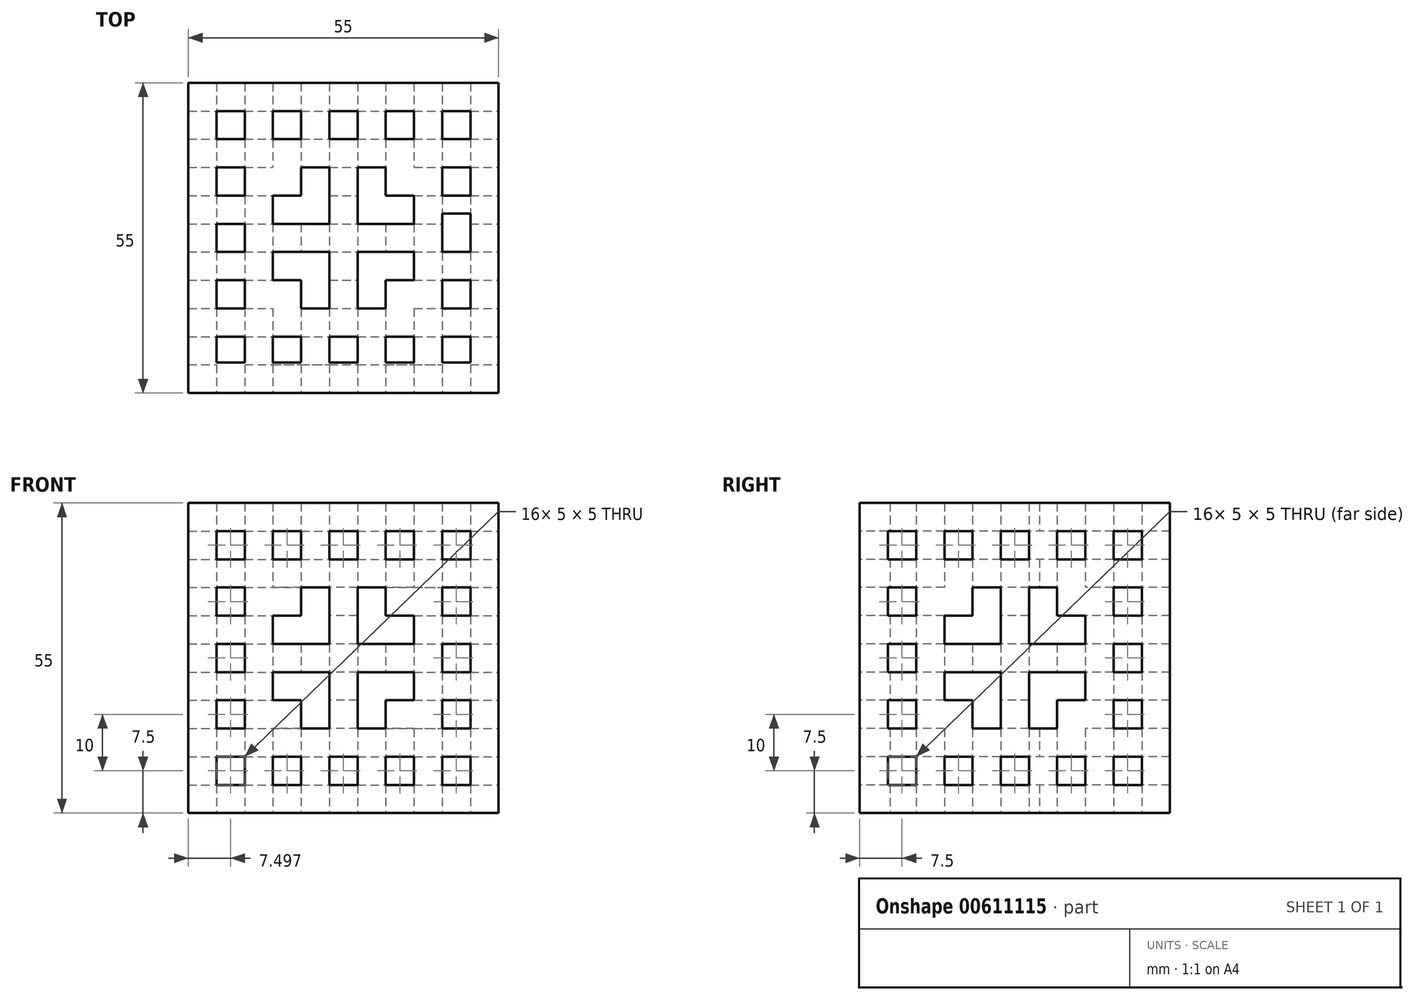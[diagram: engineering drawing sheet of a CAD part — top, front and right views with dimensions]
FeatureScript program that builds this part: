
annotation { "Feature Type Name" : "Feature", "Feature Type Description" : "" }
export const myFeature = defineFeature(function(context is Context, id is Id, definition is map)
    precondition{}
    {
        {
            var Q0;
            Q0=qCreatedBy(makeId("Top.planeOp"),FACE);
            var sketch = newSketch(context, id + "F0", { "sketchPlane" : qUnion([Q0])});
            skLineSegment(sketch, "E0.top", {"start": v(-22.46, 5.4) * mm, "end": v(-17.46, 5.4) * mm});
            skLineSegment(sketch, "E0.right", {"start": v(22.54, 40) * mm, "end": v(22.54, 35) * mm});
            skLineSegment(sketch, "E1", {"start": v(-17.46, 50) * mm, "end": v(-17.46, 45) * mm});
            skLineSegment(sketch, "E2", {"start": v(-7.46, 50) * mm, "end": v(-7.46, 45) * mm});
            skLineSegment(sketch, "E3", {"start": v(2.54, 50) * mm, "end": v(2.54, 45) * mm});
            skLineSegment(sketch, "E4", {"start": v(12.54, 50) * mm, "end": v(12.54, 45) * mm});
            skLineSegment(sketch, "E5", {"start": v(-22.46, 5.4) * mm, "end": v(-22.46, 10) * mm});
            skLineSegment(sketch, "E6", {"start": v(-12.46, 50) * mm, "end": v(-12.46, 45) * mm});
            skLineSegment(sketch, "E7", {"start": v(-2.46, 5.4) * mm, "end": v(-2.46, 10) * mm});
            skLineSegment(sketch, "E8", {"start": v(7.54, 5.4) * mm, "end": v(7.54, 10) * mm});
            skLineSegment(sketch, "E9", {"start": v(17.54, 5.4) * mm, "end": v(17.54, 10) * mm});
            skLineSegment(sketch, "E10", {"start": v(-22.46, 50) * mm, "end": v(-17.46, 50) * mm});
            skLineSegment(sketch, "E11", {"start": v(-22.46, 45) * mm, "end": v(-17.46, 45) * mm});
            skLineSegment(sketch, "E12", {"start": v(-22.46, 40) * mm, "end": v(-17.46, 40) * mm});
            skLineSegment(sketch, "E13", {"start": v(-22.46, 35) * mm, "end": v(-17.46, 35) * mm});
            skLineSegment(sketch, "E14", {"start": v(-22.46, 30) * mm, "end": v(-17.46, 30) * mm});
            skLineSegment(sketch, "E15", {"start": v(-22.46, 20) * mm, "end": v(-17.46, 20) * mm});
            skLineSegment(sketch, "E16", {"start": v(-22.46, 15) * mm, "end": v(-17.46, 15) * mm});
            skLineSegment(sketch, "E17", {"start": v(-22.46, 10) * mm, "end": v(-17.46, 10) * mm});
            skLineSegment(sketch, "E18.trimOffspring", {"start": v(-22.46, 45) * mm, "end": v(-22.46, 50) * mm});
            skLineSegment(sketch, "E19.trimOffspring", {"start": v(-17.46, 40) * mm, "end": v(-17.46, 35) * mm});
            skLineSegment(sketch, "E20.trimOffspring", {"start": v(-12.46, 45) * mm, "end": v(-7.46, 45) * mm});
            skLineSegment(sketch, "E21.trimOffspring", {"start": v(-12.46, 50) * mm, "end": v(-7.46, 50) * mm});
            skLineSegment(sketch, "E22.trimOffspring", {"start": v(-2.46, 50) * mm, "end": v(2.54, 50) * mm});
            skLineSegment(sketch, "E23.trimOffspring", {"start": v(-2.46, 45) * mm, "end": v(2.54, 45) * mm});
            skLineSegment(sketch, "E24.trimOffspring", {"start": v(-7.46, 40) * mm, "end": v(-7.46, 35) * mm});
            skLineSegment(sketch, "E25.trimOffspring", {"start": v(-12.46, 35) * mm, "end": v(-12.46, 30) * mm});
            skPoint(sketch, "E26.orphan", {"position": v(-2.46, 55.4) * mm});
            skLineSegment(sketch, "E27.trimOffspring", {"start": v(7.54, 50) * mm, "end": v(12.54, 50) * mm});
            skLineSegment(sketch, "E28.trimOffspring", {"start": v(7.54, 45) * mm, "end": v(12.54, 45) * mm});
            skLineSegment(sketch, "E29.trimOffspring", {"start": v(2.54, 40) * mm, "end": v(2.54, 30) * mm});
            skLineSegment(sketch, "E30.trimOffspring", {"start": v(-2.46, 45) * mm, "end": v(-2.46, 50) * mm});
            skLineSegment(sketch, "E31.trimOffspring", {"start": v(17.54, 50) * mm, "end": v(22.54, 50) * mm});
            skLineSegment(sketch, "E32.trimOffspring", {"start": v(17.54, 45) * mm, "end": v(22.54, 45) * mm});
            skLineSegment(sketch, "E33.trimOffspring", {"start": v(12.54, 35) * mm, "end": v(12.54, 30) * mm});
            skLineSegment(sketch, "E34.trimOffspring", {"start": v(7.54, 45) * mm, "end": v(7.54, 50) * mm});
            skLineSegment(sketch, "E35.trimOffspring", {"start": v(17.54, 45) * mm, "end": v(17.54, 50) * mm});
            skPoint(sketch, "E36.orphan", {"position": v(33.66, 8.65) * mm});
            skLineSegment(sketch, "E37", {"start": v(22.54, 50) * mm, "end": v(22.54, 45) * mm});
            skLineSegment(sketch, "E38.trimOffspring", {"start": v(-7.46, 40) * mm, "end": v(-2.46, 40) * mm});
            skLineSegment(sketch, "E39.trimOffspring", {"start": v(-22.46, 35) * mm, "end": v(-22.46, 40) * mm});
            skLineSegment(sketch, "E40.trimOffspring", {"start": v(-17.46, 30) * mm, "end": v(-17.46, 25) * mm});
            skLineSegment(sketch, "E41.trimOffspring", {"start": v(-12.46, 35) * mm, "end": v(-7.46, 35) * mm});
            skLineSegment(sketch, "E42.trimOffspring", {"start": v(-12.46, 25) * mm, "end": v(-2.46, 25) * mm});
            skLineSegment(sketch, "E43.trimOffspring", {"start": v(-17.46, 20) * mm, "end": v(-17.46, 15) * mm});
            skLineSegment(sketch, "E44.trimOffspring", {"start": v(-22.46, 25) * mm, "end": v(-22.46, 30) * mm});
            skLineSegment(sketch, "E45.trimOffspring", {"start": v(-22.46, 15) * mm, "end": v(-22.46, 20) * mm});
            skLineSegment(sketch, "E46.trimOffspring", {"start": v(-17.46, 10) * mm, "end": v(-17.46, 5.4) * mm});
            skLineSegment(sketch, "E47.trimOffspring", {"start": v(-7.46, 15) * mm, "end": v(-2.46, 15) * mm});
            skLineSegment(sketch, "E48.trimOffspring", {"start": v(-12.46, 20) * mm, "end": v(-7.46, 20) * mm});
            skLineSegment(sketch, "E49.trimOffspring", {"start": v(-12.46, 10) * mm, "end": v(-7.46, 10) * mm});
            skLineSegment(sketch, "E50.trimOffspring", {"start": v(-12.46, 5.4) * mm, "end": v(-7.46, 5.4) * mm});
            skPoint(sketch, "E51.end.orphan", {"position": v(-18.84, 9.8) * mm});
            skLineSegment(sketch, "E52", {"start": v(-22.46, 25) * mm, "end": v(-17.46, 25) * mm});
            skLineSegment(sketch, "E53.trimOffspring", {"start": v(-12.46, 10) * mm, "end": v(-12.46, 5.4) * mm});
            skLineSegment(sketch, "E54.trimOffspring", {"start": v(-7.46, 10) * mm, "end": v(-7.46, 5.4) * mm});
            skLineSegment(sketch, "E55.trimOffspring", {"start": v(-2.46, 10) * mm, "end": v(2.54, 10) * mm});
            skLineSegment(sketch, "E56.trimOffspring", {"start": v(-2.46, 5.4) * mm, "end": v(2.54, 5.4) * mm});
            skLineSegment(sketch, "E57.trimOffspring", {"start": v(-2.46, 15) * mm, "end": v(-2.46, 25) * mm});
            skLineSegment(sketch, "E58.trimOffspring", {"start": v(2.54, 10) * mm, "end": v(2.54, 5.4) * mm});
            skLineSegment(sketch, "E59.trimOffspring", {"start": v(7.54, 10) * mm, "end": v(12.54, 10) * mm});
            skLineSegment(sketch, "E60.trimOffspring", {"start": v(7.54, 5.4) * mm, "end": v(12.54, 5.4) * mm});
            skLineSegment(sketch, "E61.trimOffspring", {"start": v(7.54, 15) * mm, "end": v(7.54, 20) * mm});
            skLineSegment(sketch, "E62.trimOffspring", {"start": v(12.54, 10) * mm, "end": v(12.54, 5.4) * mm});
            skLineSegment(sketch, "E63.trimOffspring", {"start": v(17.54, 10) * mm, "end": v(22.54, 10) * mm});
            skLineSegment(sketch, "E64.trimOffspring", {"start": v(17.54, 5.4) * mm, "end": v(22.54, 5.4) * mm});
            skLineSegment(sketch, "E65.trimOffspring", {"start": v(22.54, 10) * mm, "end": v(22.54, 5.4) * mm});
            skLineSegment(sketch, "E66.trimOffspring", {"start": v(17.54, 15) * mm, "end": v(17.54, 20) * mm});
            skLineSegment(sketch, "E67.trimOffspring", {"start": v(22.54, 20) * mm, "end": v(22.54, 15) * mm});
            skLineSegment(sketch, "E68.trimOffspring", {"start": v(17.54, 25) * mm, "end": v(17.54, 31.84) * mm});
            skLineSegment(sketch, "E69.trimOffspring", {"start": v(17.54, 20) * mm, "end": v(22.54, 20) * mm});
            skLineSegment(sketch, "E70.trimOffspring", {"start": v(17.54, 15) * mm, "end": v(22.54, 15) * mm});
            skLineSegment(sketch, "E71.trimOffspring", {"start": v(17.54, 25) * mm, "end": v(22.54, 25) * mm});
            skLineSegment(sketch, "E72.trimOffspring", {"start": v(17.54, 31.84) * mm, "end": v(22.54, 31.84) * mm});
            skLineSegment(sketch, "E73.trimOffspring", {"start": v(17.54, 35) * mm, "end": v(17.54, 40) * mm});
            skLineSegment(sketch, "E74.trimOffspring", {"start": v(22.54, 31.84) * mm, "end": v(22.54, 25) * mm});
            skLineSegment(sketch, "E75.trimOffspring", {"start": v(17.54, 35) * mm, "end": v(22.54, 35) * mm});
            skLineSegment(sketch, "E76.trimOffspring", {"start": v(17.54, 40) * mm, "end": v(22.54, 40) * mm});
            skLineSegment(sketch, "E77.trimOffspring", {"start": v(-12.46, 25) * mm, "end": v(-12.46, 20) * mm});
            skLineSegment(sketch, "E78.trimOffspring", {"start": v(-7.46, 20) * mm, "end": v(-7.46, 15) * mm});
            skLineSegment(sketch, "E79.trimOffspring", {"start": v(2.54, 40) * mm, "end": v(7.54, 40) * mm});
            skLineSegment(sketch, "E80.trimOffspring", {"start": v(7.54, 35) * mm, "end": v(12.54, 35) * mm});
            skLineSegment(sketch, "E81.trimOffspring", {"start": v(12.54, 25) * mm, "end": v(12.54, 20) * mm});
            skLineSegment(sketch, "E82.trimOffspring", {"start": v(7.54, 35) * mm, "end": v(7.54, 40) * mm});
            skLineSegment(sketch, "E83.trimOffspring", {"start": v(2.54, 15) * mm, "end": v(7.54, 15) * mm});
            skLineSegment(sketch, "E84.trimOffspring", {"start": v(7.54, 20) * mm, "end": v(12.54, 20) * mm});
            skLineSegment(sketch, "E85.trimOffspring", {"start": v(2.54, 25) * mm, "end": v(12.54, 25) * mm});
            skLineSegment(sketch, "E86.trimOffspring", {"start": v(2.54, 30) * mm, "end": v(12.54, 30) * mm});
            skLineSegment(sketch, "E87.trimOffspring", {"start": v(2.54, 25) * mm, "end": v(2.54, 15) * mm});
            skLineSegment(sketch, "E88", {"start": v(-12.46, 30) * mm, "end": v(-2.46, 30) * mm});
            skLineSegment(sketch, "E89", {"start": v(-2.46, 40) * mm, "end": v(-2.46, 30) * mm});
            skPoint(sketch, "E90.start.orphan", {"position": v(-27.46, 5.4) * mm});
            skPoint(sketch, "E91.orphan", {"position": v(-23.84, 9.8) * mm});
            skLineSegment(sketch, "E92.bottom", {"start": v(-27.46, 55) * mm, "end": v(27.54, 55) * mm});
            skLineSegment(sketch, "E92.top", {"start": v(-27.46, 0) * mm, "end": v(27.54, 0) * mm});
            skLineSegment(sketch, "E92.left", {"start": v(-27.46, 55) * mm, "end": v(-27.46, 0) * mm});
            skLineSegment(sketch, "E92.right", {"start": v(27.54, 55) * mm, "end": v(27.54, 0) * mm});
            skSolve(sketch);
        }
        {
            var Q0;
            Q0=makeQuery(id+"F0.imprint","IMPRINT",FACE,{"disambiguationData":[TD([[makeQuery(id+"F0.imprint","IMPRINT",EDGE,{"derivedFrom":sQuery(id+"F0.wireOp",EDGE,"E0.top")}),-1.0]])]});
            extrude(context, id + "F1", {"entities" : qUnion([Q0]), "depth" : 55 * mm, "offsetDistance" : 25 * mm});
        }
        {
            var Q0;
            Q0=makeQuery(id+"F1.opExtrude","SWEPT_FACE",FACE,{"disambiguationData":[OSD([sQuery(id+"F0.wireOp",EDGE,"E92.top")])]});
            var sketch = newSketch(context, id + "F2", { "sketchPlane" : qUnion([Q0])});
            skLineSegment(sketch, "E93", {"start": v(-22.46, 50) * mm, "end": v(-22.46, 45) * mm});
            skLineSegment(sketch, "E94.1.0.0", {"start": v(-17.46, 50) * mm, "end": v(-17.46, 45) * mm});
            skLineSegment(sketch, "E94.2.0.0", {"start": v(-12.46, 50) * mm, "end": v(-12.46, 45) * mm});
            skLineSegment(sketch, "E94.3.0.0", {"start": v(-7.46, 50) * mm, "end": v(-7.46, 45) * mm});
            skLineSegment(sketch, "E94.4.0.0", {"start": v(-2.46, 50) * mm, "end": v(-2.46, 45) * mm});
            skLineSegment(sketch, "E94.5.0.0", {"start": v(2.54, 50) * mm, "end": v(2.54, 45) * mm});
            skLineSegment(sketch, "E94.6.0.0", {"start": v(7.54, 50) * mm, "end": v(7.54, 45) * mm});
            skLineSegment(sketch, "E94.7.0.0", {"start": v(12.54, 50) * mm, "end": v(12.54, 45) * mm});
            skLineSegment(sketch, "E94.8.0.0", {"start": v(17.54, 50) * mm, "end": v(17.54, 45) * mm});
            skLineSegment(sketch, "E94.9.0.0", {"start": v(22.54, 50) * mm, "end": v(22.54, 45) * mm});
            skLineSegment(sketch, "E94.direction1", {"start": v(-22.46, 0) * mm, "end": v(-17.46, 0) * mm, "construction": true});
            skLineSegment(sketch, "E95", {"start": v(-22.46, 5) * mm, "end": v(-17.46, 5) * mm});
            skLineSegment(sketch, "E96.0.1.0", {"start": v(-22.46, 10) * mm, "end": v(-17.46, 10) * mm});
            skLineSegment(sketch, "E96.direction1", {"start": v(-22.46, 5) * mm, "end": v(-17.46, 5) * mm, "construction": true});
            skLineSegment(sketch, "E96.direction2", {"start": v(-27.46, 5) * mm, "end": v(-27.46, 10) * mm, "construction": true});
            skLineSegment(sketch, "E97.0.0.2", {"start": v(-22.46, 15) * mm, "end": v(-17.46, 15) * mm});
            skLineSegment(sketch, "E97.0.0.3", {"start": v(-22.46, 20) * mm, "end": v(-17.46, 20) * mm});
            skLineSegment(sketch, "E97.0.0.4", {"start": v(-22.46, 25) * mm, "end": v(-17.46, 25) * mm});
            skLineSegment(sketch, "E97.0.0.5", {"start": v(-22.46, 30) * mm, "end": v(-17.46, 30) * mm});
            skLineSegment(sketch, "E97.0.0.6", {"start": v(-22.46, 35) * mm, "end": v(-17.46, 35) * mm});
            skLineSegment(sketch, "E97.0.0.7", {"start": v(-22.46, 40) * mm, "end": v(-17.46, 40) * mm});
            skLineSegment(sketch, "E97.0.0.8", {"start": v(-22.46, 45) * mm, "end": v(-17.46, 45) * mm});
            skLineSegment(sketch, "E97.0.0.9", {"start": v(-22.46, 50) * mm, "end": v(-17.46, 50) * mm});
            skPoint(sketch, "E98.orphan", {"position": v(-22.46, 55) * mm});
            skPoint(sketch, "E99.orphan", {"position": v(-17.46, 55) * mm});
            skPoint(sketch, "E100.orphan", {"position": v(-12.46, 55) * mm});
            skPoint(sketch, "E101.orphan", {"position": v(-7.46, 55) * mm});
            skPoint(sketch, "E102.orphan", {"position": v(-2.46, 55) * mm});
            skPoint(sketch, "E103.orphan", {"position": v(2.54, 55) * mm});
            skPoint(sketch, "E104.orphan", {"position": v(7.54, 55) * mm});
            skPoint(sketch, "E105.orphan", {"position": v(12.54, 55) * mm});
            skPoint(sketch, "E106.orphan", {"position": v(17.54, 55) * mm});
            skPoint(sketch, "E107.orphan", {"position": v(22.54, 55) * mm});
            skPoint(sketch, "E108.orphan", {"position": v(27.54, 50) * mm});
            skPoint(sketch, "E109.orphan", {"position": v(27.54, 45) * mm});
            skPoint(sketch, "E110.orphan", {"position": v(27.54, 40) * mm});
            skPoint(sketch, "E111.orphan", {"position": v(27.54, 35) * mm});
            skPoint(sketch, "E112.orphan", {"position": v(27.54, 30) * mm});
            skPoint(sketch, "E113.orphan", {"position": v(27.54, 25) * mm});
            skPoint(sketch, "E114.orphan", {"position": v(27.54, 20) * mm});
            skPoint(sketch, "E115.orphan", {"position": v(27.54, 10) * mm});
            skPoint(sketch, "E116.orphan", {"position": v(27.54, 15) * mm});
            skPoint(sketch, "E117.orphan", {"position": v(27.54, 5) * mm});
            skPoint(sketch, "E118.orphan", {"position": v(-27.46, 50) * mm});
            skPoint(sketch, "E119.orphan", {"position": v(-27.46, 45) * mm});
            skPoint(sketch, "E120.orphan", {"position": v(-27.46, 40) * mm});
            skPoint(sketch, "E121.orphan", {"position": v(-27.46, 35) * mm});
            skPoint(sketch, "E122.orphan", {"position": v(-27.46, 30) * mm});
            skPoint(sketch, "E123.orphan", {"position": v(-27.46, 25) * mm});
            skPoint(sketch, "E124.orphan", {"position": v(-27.46, 20) * mm});
            skPoint(sketch, "E125.orphan", {"position": v(-27.46, 15) * mm});
            skPoint(sketch, "E126.orphan", {"position": v(-12.46, 0) * mm});
            skPoint(sketch, "E127.orphan", {"position": v(-7.46, 0) * mm});
            skPoint(sketch, "E128.orphan", {"position": v(-2.46, 0) * mm});
            skPoint(sketch, "E129.orphan", {"position": v(2.54, 0) * mm});
            skPoint(sketch, "E130.orphan", {"position": v(7.54, 0) * mm});
            skPoint(sketch, "E131.orphan", {"position": v(12.54, 0) * mm});
            skPoint(sketch, "E132.orphan", {"position": v(17.54, 0) * mm});
            skPoint(sketch, "E133.orphan", {"position": v(22.54, 0) * mm});
            skLineSegment(sketch, "E134.trimOffspring", {"start": v(17.54, 5) * mm, "end": v(22.54, 5) * mm});
            skLineSegment(sketch, "E135.trimOffspring", {"start": v(17.54, 10) * mm, "end": v(22.54, 10) * mm});
            skLineSegment(sketch, "E136.trimOffspring", {"start": v(17.54, 15) * mm, "end": v(22.54, 15) * mm});
            skLineSegment(sketch, "E137.trimOffspring", {"start": v(17.54, 30) * mm, "end": v(22.54, 30) * mm});
            skLineSegment(sketch, "E138.trimOffspring", {"start": v(17.54, 25) * mm, "end": v(22.54, 25) * mm});
            skLineSegment(sketch, "E139.trimOffspring", {"start": v(17.54, 20) * mm, "end": v(22.54, 20) * mm});
            skLineSegment(sketch, "E140.trimOffspring", {"start": v(17.54, 40) * mm, "end": v(22.54, 40) * mm});
            skLineSegment(sketch, "E141.trimOffspring", {"start": v(17.54, 35) * mm, "end": v(22.54, 35) * mm});
            skLineSegment(sketch, "E142.trimOffspring", {"start": v(17.54, 45) * mm, "end": v(22.54, 45) * mm});
            skLineSegment(sketch, "E143.trimOffspring", {"start": v(17.54, 50) * mm, "end": v(22.54, 50) * mm});
            skLineSegment(sketch, "E144.trimOffspring", {"start": v(17.54, 40) * mm, "end": v(17.54, 35) * mm});
            skLineSegment(sketch, "E145.trimOffspring", {"start": v(22.54, 40) * mm, "end": v(22.54, 35) * mm});
            skLineSegment(sketch, "E146.trimOffspring", {"start": v(22.54, 30) * mm, "end": v(22.54, 25) * mm});
            skLineSegment(sketch, "E147.trimOffspring", {"start": v(17.54, 30) * mm, "end": v(17.54, 25) * mm});
            skLineSegment(sketch, "E148.trimOffspring", {"start": v(17.54, 20) * mm, "end": v(17.54, 15) * mm});
            skLineSegment(sketch, "E149.trimOffspring", {"start": v(22.54, 20) * mm, "end": v(22.54, 15) * mm});
            skLineSegment(sketch, "E150.trimOffspring", {"start": v(22.54, 10) * mm, "end": v(22.54, 5) * mm});
            skLineSegment(sketch, "E151.trimOffspring", {"start": v(17.54, 10) * mm, "end": v(17.54, 5) * mm});
            skLineSegment(sketch, "E152.trimOffspring", {"start": v(12.54, 35) * mm, "end": v(12.54, 30) * mm});
            skLineSegment(sketch, "E153.trimOffspring", {"start": v(7.54, 40) * mm, "end": v(7.54, 35) * mm});
            skLineSegment(sketch, "E154.trimOffspring", {"start": v(2.54, 40) * mm, "end": v(2.54, 30) * mm});
            skLineSegment(sketch, "E155.trimOffspring", {"start": v(-7.46, 40) * mm, "end": v(-7.46, 35) * mm});
            skLineSegment(sketch, "E156.trimOffspring", {"start": v(-2.46, 40) * mm, "end": v(-2.46, 30) * mm});
            skLineSegment(sketch, "E157.trimOffspring", {"start": v(-12.46, 35) * mm, "end": v(-12.46, 30) * mm});
            skLineSegment(sketch, "E158.trimOffspring", {"start": v(-17.46, 40) * mm, "end": v(-17.46, 35) * mm});
            skLineSegment(sketch, "E159.trimOffspring", {"start": v(-12.46, 45) * mm, "end": v(-7.46, 45) * mm});
            skLineSegment(sketch, "E160.trimOffspring", {"start": v(-12.46, 50) * mm, "end": v(-7.46, 50) * mm});
            skLineSegment(sketch, "E161.trimOffspring", {"start": v(-2.46, 45) * mm, "end": v(2.54, 45) * mm});
            skLineSegment(sketch, "E162.trimOffspring", {"start": v(-2.46, 50) * mm, "end": v(2.54, 50) * mm});
            skLineSegment(sketch, "E163.trimOffspring", {"start": v(7.54, 45) * mm, "end": v(12.54, 45) * mm});
            skLineSegment(sketch, "E164.trimOffspring", {"start": v(7.54, 50) * mm, "end": v(12.54, 50) * mm});
            skLineSegment(sketch, "E165.trimOffspring", {"start": v(-22.46, 40) * mm, "end": v(-22.46, 35) * mm});
            skLineSegment(sketch, "E166.trimOffspring", {"start": v(-7.46, 40) * mm, "end": v(-2.46, 40) * mm});
            skLineSegment(sketch, "E167.trimOffspring", {"start": v(-12.46, 35) * mm, "end": v(-7.46, 35) * mm});
            skLineSegment(sketch, "E168.trimOffspring", {"start": v(-12.46, 30) * mm, "end": v(-2.46, 30) * mm});
            skLineSegment(sketch, "E169.trimOffspring", {"start": v(-12.46, 25) * mm, "end": v(-2.46, 25) * mm});
            skLineSegment(sketch, "E170.trimOffspring", {"start": v(-12.46, 20) * mm, "end": v(-7.46, 20) * mm});
            skLineSegment(sketch, "E171.trimOffspring", {"start": v(-7.46, 15) * mm, "end": v(-2.46, 15) * mm});
            skLineSegment(sketch, "E172.trimOffspring", {"start": v(-12.46, 10) * mm, "end": v(-7.46, 10) * mm});
            skLineSegment(sketch, "E173.trimOffspring", {"start": v(-12.46, 5) * mm, "end": v(-7.46, 5) * mm, "construction": true});
            skLineSegment(sketch, "E174.trimOffspring", {"start": v(-12.46, 5) * mm, "end": v(-7.46, 5) * mm});
            skLineSegment(sketch, "E175.trimOffspring", {"start": v(-12.46, 10) * mm, "end": v(-12.46, 5) * mm});
            skLineSegment(sketch, "E176.trimOffspring", {"start": v(-7.46, 10) * mm, "end": v(-7.46, 5) * mm});
            skLineSegment(sketch, "E177.trimOffspring", {"start": v(-2.46, 10) * mm, "end": v(-2.46, 5) * mm});
            skLineSegment(sketch, "E178.trimOffspring", {"start": v(2.54, 10) * mm, "end": v(2.54, 5) * mm});
            skLineSegment(sketch, "E179.trimOffspring", {"start": v(7.54, 10) * mm, "end": v(7.54, 5) * mm});
            skLineSegment(sketch, "E180.trimOffspring", {"start": v(12.54, 10) * mm, "end": v(12.54, 5) * mm});
            skLineSegment(sketch, "E181.trimOffspring", {"start": v(7.54, 10) * mm, "end": v(12.54, 10) * mm});
            skLineSegment(sketch, "E182.trimOffspring", {"start": v(7.54, 5) * mm, "end": v(12.54, 5) * mm});
            skLineSegment(sketch, "E183.trimOffspring", {"start": v(-2.46, 10) * mm, "end": v(2.54, 10) * mm});
            skLineSegment(sketch, "E184.trimOffspring", {"start": v(-17.46, 10) * mm, "end": v(-17.46, 5) * mm});
            skLineSegment(sketch, "E185.trimOffspring", {"start": v(-22.46, 10) * mm, "end": v(-22.46, 5) * mm});
            skLineSegment(sketch, "E186.trimOffspring", {"start": v(-22.46, 20) * mm, "end": v(-22.46, 15) * mm});
            skLineSegment(sketch, "E187.trimOffspring", {"start": v(-17.46, 20) * mm, "end": v(-17.46, 15) * mm});
            skLineSegment(sketch, "E188.trimOffspring", {"start": v(-17.46, 30) * mm, "end": v(-17.46, 25) * mm});
            skLineSegment(sketch, "E189.trimOffspring", {"start": v(-22.46, 30) * mm, "end": v(-22.46, 25) * mm});
            skLineSegment(sketch, "E190.trimOffspring", {"start": v(2.54, 40) * mm, "end": v(7.54, 40) * mm});
            skLineSegment(sketch, "E191.trimOffspring", {"start": v(7.54, 35) * mm, "end": v(12.54, 35) * mm});
            skLineSegment(sketch, "E192.trimOffspring", {"start": v(2.54, 30) * mm, "end": v(12.54, 30) * mm});
            skLineSegment(sketch, "E193.trimOffspring", {"start": v(2.54, 25) * mm, "end": v(12.54, 25) * mm});
            skLineSegment(sketch, "E194.trimOffspring", {"start": v(7.54, 20) * mm, "end": v(12.54, 20) * mm});
            skLineSegment(sketch, "E195.trimOffspring", {"start": v(2.54, 15) * mm, "end": v(7.54, 15) * mm});
            skLineSegment(sketch, "E196.trimOffspring", {"start": v(12.54, 25) * mm, "end": v(12.54, 20) * mm});
            skLineSegment(sketch, "E197.trimOffspring", {"start": v(7.54, 20) * mm, "end": v(7.54, 15) * mm});
            skLineSegment(sketch, "E198.trimOffspring", {"start": v(2.54, 25) * mm, "end": v(2.54, 15) * mm});
            skLineSegment(sketch, "E199.trimOffspring", {"start": v(-2.46, 25) * mm, "end": v(-2.46, 15) * mm});
            skLineSegment(sketch, "E200.trimOffspring", {"start": v(-7.46, 20) * mm, "end": v(-7.46, 15) * mm});
            skLineSegment(sketch, "E201.trimOffspring", {"start": v(-12.46, 25) * mm, "end": v(-12.46, 20) * mm});
            skLineSegment(sketch, "E202.trimOffspring", {"start": v(-2.46, 5) * mm, "end": v(2.54, 5) * mm});
            skSolve(sketch);
        }
        {
            var Q0;
            Q0=makeQuery(id+"F2.imprint","IMPRINT",FACE,{"disambiguationData":[TD([[makeQuery(id+"F2.imprint","IMPRINT",EDGE,{"derivedFrom":sQuery(id+"F2.wireOp",EDGE,"E93")}),1.0]])]});
            var Q1;
            Q1=makeQuery(id+"F2.imprint","IMPRINT",FACE,{"disambiguationData":[TD([[makeQuery(id+"F2.imprint","IMPRINT",EDGE,{"derivedFrom":sQuery(id+"F2.wireOp",EDGE,"E94.2.0.0")}),1.0]])]});
            var Q2;
            Q2=makeQuery(id+"F2.imprint","IMPRINT",FACE,{"disambiguationData":[TD([[makeQuery(id+"F2.imprint","IMPRINT",EDGE,{"derivedFrom":sQuery(id+"F2.wireOp",EDGE,"E94.4.0.0")}),1.0]])]});
            var Q3;
            Q3=makeQuery(id+"F2.imprint","IMPRINT",FACE,{"disambiguationData":[TD([[makeQuery(id+"F2.imprint","IMPRINT",EDGE,{"derivedFrom":sQuery(id+"F2.wireOp",EDGE,"E94.6.0.0")}),1.0]])]});
            var Q4;
            Q4=makeQuery(id+"F2.imprint","IMPRINT",FACE,{"disambiguationData":[TD([[makeQuery(id+"F2.imprint","IMPRINT",EDGE,{"derivedFrom":sQuery(id+"F2.wireOp",EDGE,"E94.8.0.0")}),1.0]])]});
            var Q5;
            Q5=makeQuery(id+"F2.imprint","IMPRINT",FACE,{"disambiguationData":[TD([[makeQuery(id+"F2.imprint","IMPRINT",EDGE,{"derivedFrom":sQuery(id+"F2.wireOp",EDGE,"E140.trimOffspring")}),-1.0]])]});
            var Q6;
            Q6=makeQuery(id+"F2.imprint","IMPRINT",FACE,{"disambiguationData":[TD([[makeQuery(id+"F2.imprint","IMPRINT",EDGE,{"derivedFrom":sQuery(id+"F2.wireOp",EDGE,"E137.trimOffspring")}),-1.0]])]});
            var Q7;
            Q7=makeQuery(id+"F2.imprint","IMPRINT",FACE,{"disambiguationData":[TD([[makeQuery(id+"F2.imprint","IMPRINT",EDGE,{"derivedFrom":sQuery(id+"F2.wireOp",EDGE,"E136.trimOffspring")}),1.0]])]});
            var Q8;
            Q8=makeQuery(id+"F2.imprint","IMPRINT",FACE,{"disambiguationData":[TD([[makeQuery(id+"F2.imprint","IMPRINT",EDGE,{"derivedFrom":sQuery(id+"F2.wireOp",EDGE,"E134.trimOffspring")}),1.0]])]});
            var Q9;
            Q9=makeQuery(id+"F2.imprint","IMPRINT",FACE,{"disambiguationData":[TD([[makeQuery(id+"F2.imprint","IMPRINT",EDGE,{"derivedFrom":sQuery(id+"F2.wireOp",EDGE,"E179.trimOffspring")}),1.0]])]});
            var Q10;
            Q10=makeQuery(id+"F2.imprint","IMPRINT",FACE,{"disambiguationData":[TD([[makeQuery(id+"F2.imprint","IMPRINT",EDGE,{"derivedFrom":sQuery(id+"F2.wireOp",EDGE,"E177.trimOffspring")}),1.0]])]});
            var Q11;
            Q11=makeQuery(id+"F2.imprint","IMPRINT",FACE,{"disambiguationData":[TD([[makeQuery(id+"F2.imprint","IMPRINT",EDGE,{"derivedFrom":sQuery(id+"F2.wireOp",EDGE,"E172.trimOffspring")}),-1.0]])]});
            var Q12;
            Q12=makeQuery(id+"F2.imprint","IMPRINT",FACE,{"disambiguationData":[TD([[makeQuery(id+"F2.imprint","IMPRINT",EDGE,{"derivedFrom":sQuery(id+"F2.wireOp",EDGE,"E95")}),1.0]])]});
            var Q13;
            Q13=makeQuery(id+"F2.imprint","IMPRINT",FACE,{"disambiguationData":[TD([[makeQuery(id+"F2.imprint","IMPRINT",EDGE,{"derivedFrom":sQuery(id+"F2.wireOp",EDGE,"E97.0.0.2")}),1.0]])]});
            var Q14;
            Q14=makeQuery(id+"F2.imprint","IMPRINT",FACE,{"disambiguationData":[TD([[makeQuery(id+"F2.imprint","IMPRINT",EDGE,{"derivedFrom":sQuery(id+"F2.wireOp",EDGE,"E97.0.0.4")}),1.0]])]});
            var Q15;
            Q15=makeQuery(id+"F2.imprint","IMPRINT",FACE,{"disambiguationData":[TD([[makeQuery(id+"F2.imprint","IMPRINT",EDGE,{"derivedFrom":sQuery(id+"F2.wireOp",EDGE,"E97.0.0.6")}),1.0]])]});
            var Q16;
            Q16=makeQuery(id+"F2.imprint","IMPRINT",FACE,{"disambiguationData":[TD([[makeQuery(id+"F2.imprint","IMPRINT",EDGE,{"derivedFrom":sQuery(id+"F2.wireOp",EDGE,"E155.trimOffspring")}),1.0]])]});
            var Q17;
            Q17=makeQuery(id+"F2.imprint","IMPRINT",FACE,{"disambiguationData":[TD([[makeQuery(id+"F2.imprint","IMPRINT",EDGE,{"derivedFrom":sQuery(id+"F2.wireOp",EDGE,"E152.trimOffspring")}),-1.0]])]});
            var Q18;
            Q18=makeQuery(id+"F2.imprint","IMPRINT",FACE,{"disambiguationData":[TD([[makeQuery(id+"F2.imprint","IMPRINT",EDGE,{"derivedFrom":sQuery(id+"F2.wireOp",EDGE,"E193.trimOffspring")}),-1.0]])]});
            var Q19;
            Q19=makeQuery(id+"F2.imprint","IMPRINT",FACE,{"disambiguationData":[TD([[makeQuery(id+"F2.imprint","IMPRINT",EDGE,{"derivedFrom":sQuery(id+"F2.wireOp",EDGE,"E169.trimOffspring")}),-1.0]])]});
            extrude(context, id + "F3", {"entities" : qUnion([Q0, Q1, Q2, Q3, Q4, Q5, Q6, Q7, Q8, Q9, Q10, Q11, Q12, Q13, Q14, Q15, Q16, Q17, Q18, Q19]), "operationType" : NewBodyOperationType.REMOVE, "oppositeDirection" : true, "depth" : 55 * mm, "offsetDistance" : 25 * mm});
        }
        {
            var Q0;
            Q0=makeQuery(id+"F1.opExtrude","SWEPT_FACE",FACE,{"disambiguationData":[OSD([sQuery(id+"F0.wireOp",EDGE,"E92.right")])]});
            var sketch = newSketch(context, id + "F4", { "sketchPlane" : qUnion([Q0])});
            skLineSegment(sketch, "E203", {"start": v(5, 50) * mm, "end": v(5, 45) * mm});
            skLineSegment(sketch, "E204.1.0.0", {"start": v(10, 50) * mm, "end": v(10, 45) * mm});
            skLineSegment(sketch, "E204.2.0.0", {"start": v(15, 50) * mm, "end": v(15, 45) * mm});
            skLineSegment(sketch, "E204.3.0.0", {"start": v(20, 50) * mm, "end": v(20, 45) * mm});
            skLineSegment(sketch, "E204.4.0.0", {"start": v(25, 50) * mm, "end": v(25, 45) * mm});
            skLineSegment(sketch, "E204.5.0.0", {"start": v(30, 40) * mm, "end": v(30, 30) * mm});
            skLineSegment(sketch, "E204.6.0.0", {"start": v(35, 50) * mm, "end": v(35, 45) * mm});
            skLineSegment(sketch, "E204.7.0.0", {"start": v(40, 50) * mm, "end": v(40, 45) * mm});
            skLineSegment(sketch, "E204.8.0.0", {"start": v(45, 50) * mm, "end": v(45, 45) * mm});
            skLineSegment(sketch, "E204.9.0.0", {"start": v(50, 50) * mm, "end": v(50, 45) * mm});
            skLineSegment(sketch, "E204.direction1", {"start": v(5, 0) * mm, "end": v(10, 0) * mm, "construction": true});
            skLineSegment(sketch, "E205.0.1.0", {"start": v(5, 45) * mm, "end": v(10, 45) * mm});
            skLineSegment(sketch, "E205.0.2.0", {"start": v(5, 40) * mm, "end": v(10, 40) * mm});
            skLineSegment(sketch, "E205.0.3.0", {"start": v(5, 35) * mm, "end": v(10, 35) * mm});
            skLineSegment(sketch, "E205.0.4.0", {"start": v(5, 30) * mm, "end": v(10, 30) * mm});
            skLineSegment(sketch, "E205.0.5.0", {"start": v(5, 25) * mm, "end": v(10, 25) * mm});
            skLineSegment(sketch, "E205.0.6.0", {"start": v(5, 20) * mm, "end": v(10, 20) * mm});
            skLineSegment(sketch, "E205.0.7.0", {"start": v(5, 15) * mm, "end": v(10, 15) * mm});
            skLineSegment(sketch, "E205.0.8.0", {"start": v(5, 10) * mm, "end": v(10, 10) * mm});
            skLineSegment(sketch, "E205.0.9.0", {"start": v(5, 5) * mm, "end": v(10, 5) * mm});
            skLineSegment(sketch, "E205.direction2", {"start": v(0, 50) * mm, "end": v(0, 45) * mm, "construction": true});
            skPoint(sketch, "E206.orphan", {"position": v(5, 55) * mm});
            skPoint(sketch, "E207.orphan", {"position": v(10, 55) * mm});
            skPoint(sketch, "E208.orphan", {"position": v(0, 40) * mm});
            skPoint(sketch, "E209.orphan", {"position": v(0, 35) * mm});
            skPoint(sketch, "E210.orphan", {"position": v(0, 30) * mm});
            skPoint(sketch, "E211.orphan", {"position": v(0, 25) * mm});
            skPoint(sketch, "E212.orphan", {"position": v(0, 20) * mm});
            skPoint(sketch, "E213.orphan", {"position": v(0, 15) * mm});
            skPoint(sketch, "E214.orphan", {"position": v(0, 10) * mm});
            skPoint(sketch, "E215.orphan", {"position": v(0, 5) * mm});
            skPoint(sketch, "E216.orphan", {"position": v(15, 0) * mm});
            skPoint(sketch, "E217.orphan", {"position": v(20, 0) * mm});
            skPoint(sketch, "E218.orphan", {"position": v(25, 0) * mm});
            skPoint(sketch, "E219.orphan", {"position": v(30, 0) * mm});
            skPoint(sketch, "E220.orphan", {"position": v(35, 0) * mm});
            skPoint(sketch, "E221.orphan", {"position": v(40, 0) * mm});
            skPoint(sketch, "E222.orphan", {"position": v(45, 0) * mm});
            skPoint(sketch, "E223.orphan", {"position": v(50, 0) * mm});
            skPoint(sketch, "E224.orphan", {"position": v(55, 5) * mm});
            skPoint(sketch, "E225.orphan", {"position": v(55, 15) * mm});
            skPoint(sketch, "E226.orphan", {"position": v(55, 10) * mm});
            skPoint(sketch, "E227.orphan", {"position": v(55, 20) * mm});
            skPoint(sketch, "E228.orphan", {"position": v(55, 25) * mm});
            skPoint(sketch, "E229.orphan", {"position": v(55, 30) * mm});
            skPoint(sketch, "E230.orphan", {"position": v(55, 35) * mm});
            skPoint(sketch, "E231.orphan", {"position": v(55, 40) * mm});
            skPoint(sketch, "E232.orphan", {"position": v(55, 45) * mm});
            skPoint(sketch, "E233.orphan", {"position": v(55, 50) * mm});
            skPoint(sketch, "E234.orphan", {"position": v(50, 55) * mm});
            skPoint(sketch, "E235.orphan", {"position": v(45, 55) * mm});
            skPoint(sketch, "E236.orphan", {"position": v(40, 55) * mm});
            skPoint(sketch, "E237.orphan", {"position": v(35, 55) * mm});
            skPoint(sketch, "E238.orphan", {"position": v(30, 55) * mm});
            skPoint(sketch, "E239.orphan", {"position": v(20, 55) * mm});
            skPoint(sketch, "E240.orphan", {"position": v(25, 55) * mm});
            skPoint(sketch, "E241.orphan", {"position": v(15, 55) * mm});
            skLineSegment(sketch, "E242.trimOffspring", {"start": v(15, 50) * mm, "end": v(20, 50) * mm, "construction": true});
            skLineSegment(sketch, "E243.trimOffspring", {"start": v(15, 45) * mm, "end": v(20, 45) * mm});
            skLineSegment(sketch, "E244.trimOffspring", {"start": v(15, 50) * mm, "end": v(20, 50) * mm});
            skLineSegment(sketch, "E245.trimOffspring", {"start": v(20, 40) * mm, "end": v(25, 40) * mm});
            skLineSegment(sketch, "E246.trimOffspring", {"start": v(15, 35) * mm, "end": v(20, 35) * mm});
            skLineSegment(sketch, "E247.trimOffspring", {"start": v(15, 30) * mm, "end": v(25, 30) * mm});
            skLineSegment(sketch, "E248.trimOffspring", {"start": v(15, 25) * mm, "end": v(25, 25) * mm});
            skLineSegment(sketch, "E249.trimOffspring", {"start": v(15, 20) * mm, "end": v(20, 20) * mm});
            skLineSegment(sketch, "E250.trimOffspring", {"start": v(20, 15) * mm, "end": v(25, 15) * mm});
            skLineSegment(sketch, "E251.trimOffspring", {"start": v(15, 10) * mm, "end": v(20, 10) * mm});
            skLineSegment(sketch, "E252.trimOffspring", {"start": v(15, 5) * mm, "end": v(20, 5) * mm});
            skLineSegment(sketch, "E253.trimOffspring", {"start": v(15, 10) * mm, "end": v(15, 5) * mm});
            skLineSegment(sketch, "E254.trimOffspring", {"start": v(20, 10) * mm, "end": v(20, 5) * mm});
            skLineSegment(sketch, "E255", {"start": v(20, 20) * mm, "end": v(20, 15) * mm});
            skLineSegment(sketch, "E256.trimOffspring", {"start": v(25, 10) * mm, "end": v(25, 5) * mm});
            skLineSegment(sketch, "E257.trimOffspring", {"start": v(30, 10) * mm, "end": v(30, 5) * mm});
            skLineSegment(sketch, "E258.trimOffspring", {"start": v(35, 10) * mm, "end": v(35, 5) * mm});
            skLineSegment(sketch, "E259.trimOffspring", {"start": v(40, 10) * mm, "end": v(40, 5) * mm});
            skLineSegment(sketch, "E260.trimOffspring", {"start": v(45, 10) * mm, "end": v(45, 5) * mm});
            skLineSegment(sketch, "E261.trimOffspring", {"start": v(50, 10) * mm, "end": v(50, 5) * mm});
            skLineSegment(sketch, "E262.trimOffspring", {"start": v(45, 15) * mm, "end": v(50, 15) * mm});
            skLineSegment(sketch, "E263.trimOffspring", {"start": v(45, 20) * mm, "end": v(50, 20) * mm});
            skLineSegment(sketch, "E264.trimOffspring", {"start": v(45, 25) * mm, "end": v(50, 25) * mm});
            skLineSegment(sketch, "E265.trimOffspring", {"start": v(45, 30) * mm, "end": v(50, 30) * mm});
            skLineSegment(sketch, "E266.trimOffspring", {"start": v(45, 35) * mm, "end": v(50, 35) * mm});
            skLineSegment(sketch, "E267.trimOffspring", {"start": v(45, 40) * mm, "end": v(50, 40) * mm});
            skLineSegment(sketch, "E268.trimOffspring", {"start": v(45, 45) * mm, "end": v(50, 45) * mm});
            skLineSegment(sketch, "E269.trimOffspring", {"start": v(45, 50) * mm, "end": v(50, 50) * mm});
            skLineSegment(sketch, "E270.trimOffspring", {"start": v(40, 35) * mm, "end": v(40, 30) * mm});
            skLineSegment(sketch, "E271.trimOffspring", {"start": v(35, 40) * mm, "end": v(35, 35) * mm});
            skLineSegment(sketch, "E272.trimOffspring", {"start": v(25, 40) * mm, "end": v(25, 30) * mm});
            skLineSegment(sketch, "E273.trimOffspring", {"start": v(20, 40) * mm, "end": v(20, 35) * mm});
            skLineSegment(sketch, "E274.trimOffspring", {"start": v(15, 35) * mm, "end": v(15, 30) * mm});
            skLineSegment(sketch, "E275.trimOffspring", {"start": v(5, 40) * mm, "end": v(5, 35) * mm});
            skLineSegment(sketch, "E276.trimOffspring", {"start": v(5, 30) * mm, "end": v(5, 25) * mm});
            skLineSegment(sketch, "E277.trimOffspring", {"start": v(10, 30) * mm, "end": v(10, 25) * mm});
            skLineSegment(sketch, "E278.trimOffspring", {"start": v(10, 20) * mm, "end": v(10, 15) * mm});
            skLineSegment(sketch, "E279.trimOffspring", {"start": v(5, 20) * mm, "end": v(5, 15) * mm});
            skLineSegment(sketch, "E280.trimOffspring", {"start": v(5, 10) * mm, "end": v(5, 5) * mm});
            skLineSegment(sketch, "E281.trimOffspring", {"start": v(10, 10) * mm, "end": v(10, 5) * mm});
            skLineSegment(sketch, "E282.trimOffspring", {"start": v(25, 10) * mm, "end": v(30, 10) * mm});
            skLineSegment(sketch, "E283.trimOffspring", {"start": v(25, 5) * mm, "end": v(30, 5) * mm});
            skLineSegment(sketch, "E284.trimOffspring", {"start": v(35, 10) * mm, "end": v(40, 10) * mm});
            skLineSegment(sketch, "E285.trimOffspring", {"start": v(35, 5) * mm, "end": v(40, 5) * mm});
            skLineSegment(sketch, "E286.trimOffspring", {"start": v(45, 5) * mm, "end": v(50, 5) * mm});
            skLineSegment(sketch, "E287.trimOffspring", {"start": v(45, 10) * mm, "end": v(50, 10) * mm});
            skLineSegment(sketch, "E288.trimOffspring", {"start": v(45, 20) * mm, "end": v(45, 15) * mm});
            skLineSegment(sketch, "E289.trimOffspring", {"start": v(50, 20) * mm, "end": v(50, 15) * mm});
            skLineSegment(sketch, "E290.trimOffspring", {"start": v(45, 30) * mm, "end": v(45, 25) * mm});
            skLineSegment(sketch, "E291.trimOffspring", {"start": v(50, 30) * mm, "end": v(50, 25) * mm});
            skLineSegment(sketch, "E292.trimOffspring", {"start": v(45, 40) * mm, "end": v(45, 35) * mm});
            skLineSegment(sketch, "E293.trimOffspring", {"start": v(50, 40) * mm, "end": v(50, 35) * mm});
            skLineSegment(sketch, "E294.trimOffspring", {"start": v(30, 40) * mm, "end": v(35, 40) * mm});
            skLineSegment(sketch, "E295.trimOffspring", {"start": v(35, 35) * mm, "end": v(40, 35) * mm});
            skLineSegment(sketch, "E296.trimOffspring", {"start": v(30, 30) * mm, "end": v(40, 30) * mm});
            skLineSegment(sketch, "E297.trimOffspring", {"start": v(30, 25) * mm, "end": v(40, 25) * mm});
            skLineSegment(sketch, "E298.trimOffspring", {"start": v(35, 20) * mm, "end": v(40, 20) * mm});
            skLineSegment(sketch, "E299.trimOffspring", {"start": v(30, 15) * mm, "end": v(35, 15) * mm});
            skLineSegment(sketch, "E300.trimOffspring", {"start": v(15, 25) * mm, "end": v(15, 20) * mm});
            skLineSegment(sketch, "E301.trimOffspring", {"start": v(10, 40) * mm, "end": v(10, 35) * mm});
            skLineSegment(sketch, "E302.trimOffspring", {"start": v(25, 25) * mm, "end": v(25, 15) * mm});
            skLineSegment(sketch, "E303.trimOffspring", {"start": v(30, 25) * mm, "end": v(30, 15) * mm});
            skLineSegment(sketch, "E304.trimOffspring", {"start": v(35, 20) * mm, "end": v(35, 15) * mm});
            skLineSegment(sketch, "E305.trimOffspring", {"start": v(40, 25) * mm, "end": v(40, 20) * mm});
            skLineSegment(sketch, "E306", {"start": v(30, 50) * mm, "end": v(30, 45) * mm});
            skLineSegment(sketch, "E307.trimOffspring", {"start": v(25, 45) * mm, "end": v(30, 45) * mm});
            skLineSegment(sketch, "E308.trimOffspring", {"start": v(35, 50) * mm, "end": v(40, 50) * mm});
            skLineSegment(sketch, "E309.trimOffspring", {"start": v(35, 45) * mm, "end": v(40, 45) * mm});
            skLineSegment(sketch, "E310.trimOffspring", {"start": v(25, 50) * mm, "end": v(30, 50) * mm});
            skLineSegment(sketch, "E311", {"start": v(5, 50) * mm, "end": v(10, 50) * mm});
            skSolve(sketch);
        }
        {
            var Q0;
            Q0 = qSketchRegion(id + "F4", true);
            var Q1;
            Q1=makeQuery(id+"F4.imprint","IMPRINT",FACE,{"disambiguationData":[TD([[makeQuery(id+"F4.imprint","IMPRINT",EDGE,{"derivedFrom":sQuery(id+"F4.wireOp",EDGE,"E203")}),1.0]])]});
            extrude(context, id + "F5", {"entities" : qUnion([Q0, Q1]), "operationType" : NewBodyOperationType.REMOVE, "oppositeDirection" : true, "depth" : 55 * mm, "offsetDistance" : 25 * mm});
        }
    });
